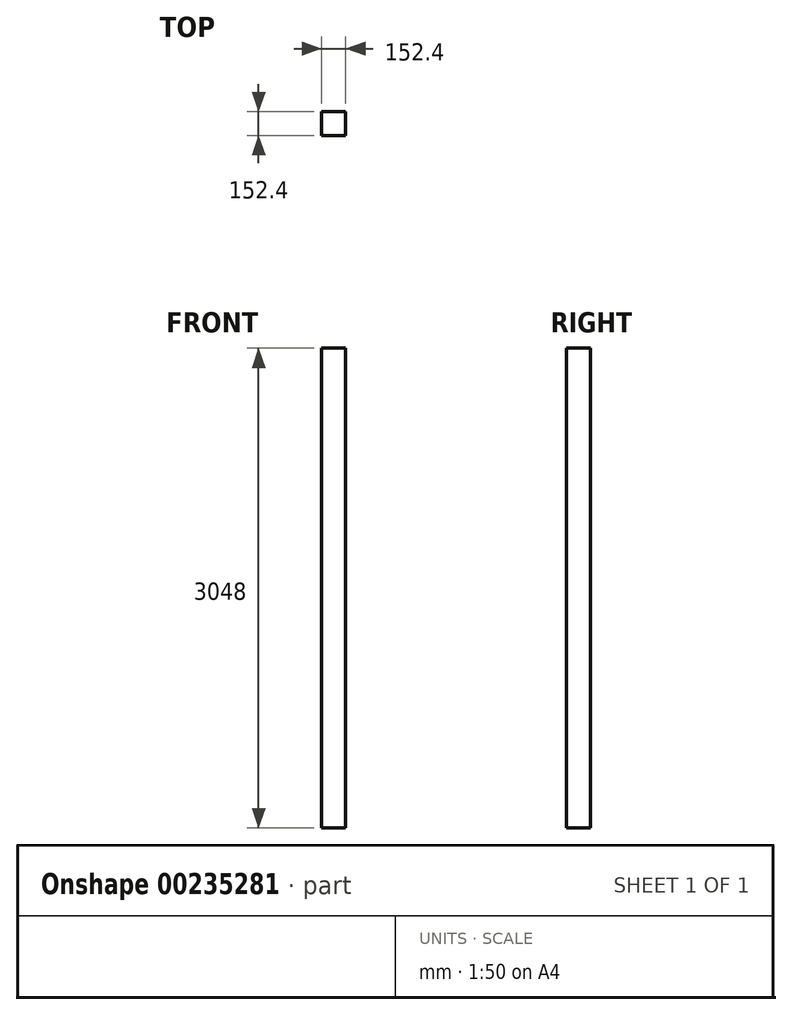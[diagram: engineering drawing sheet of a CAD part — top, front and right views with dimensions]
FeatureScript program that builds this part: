
annotation { "Feature Type Name" : "Feature", "Feature Type Description" : "" }
export const myFeature = defineFeature(function(context is Context, id is Id, definition is map)
    precondition{}
    {
        {
            var Q0;
            Q0=qCreatedBy(makeId("Top.planeOp"),FACE);
            var sketch = newSketch(context, id + "F0", { "sketchPlane" : qUnion([Q0])});
            skLineSegment(sketch, "E0", {"start": v(0, 0) * mm, "end": v(152.4, 0) * mm});
            skLineSegment(sketch, "E1", {"start": v(152.4, 0) * mm, "end": v(152.4, 152.4) * mm});
            skLineSegment(sketch, "E2", {"start": v(152.4, 152.4) * mm, "end": v(0, 152.4) * mm});
            skLineSegment(sketch, "E3", {"start": v(0, 152.4) * mm, "end": v(0, 0) * mm});
            skSolve(sketch);
        }
        {
            var Q0;
            Q0=makeQuery(id+"F0.imprint","IMPRINT",FACE,{"disambiguationData":[TD([[makeQuery(id+"F0.imprint","IMPRINT",EDGE,{"derivedFrom":sQuery(id+"F0.wireOp",EDGE,"E0")}),1.0]])]});
            extrude(context, id + "F1", {"entities" : qUnion([Q0]), "depth" : 3048 * mm});
        }
    });
